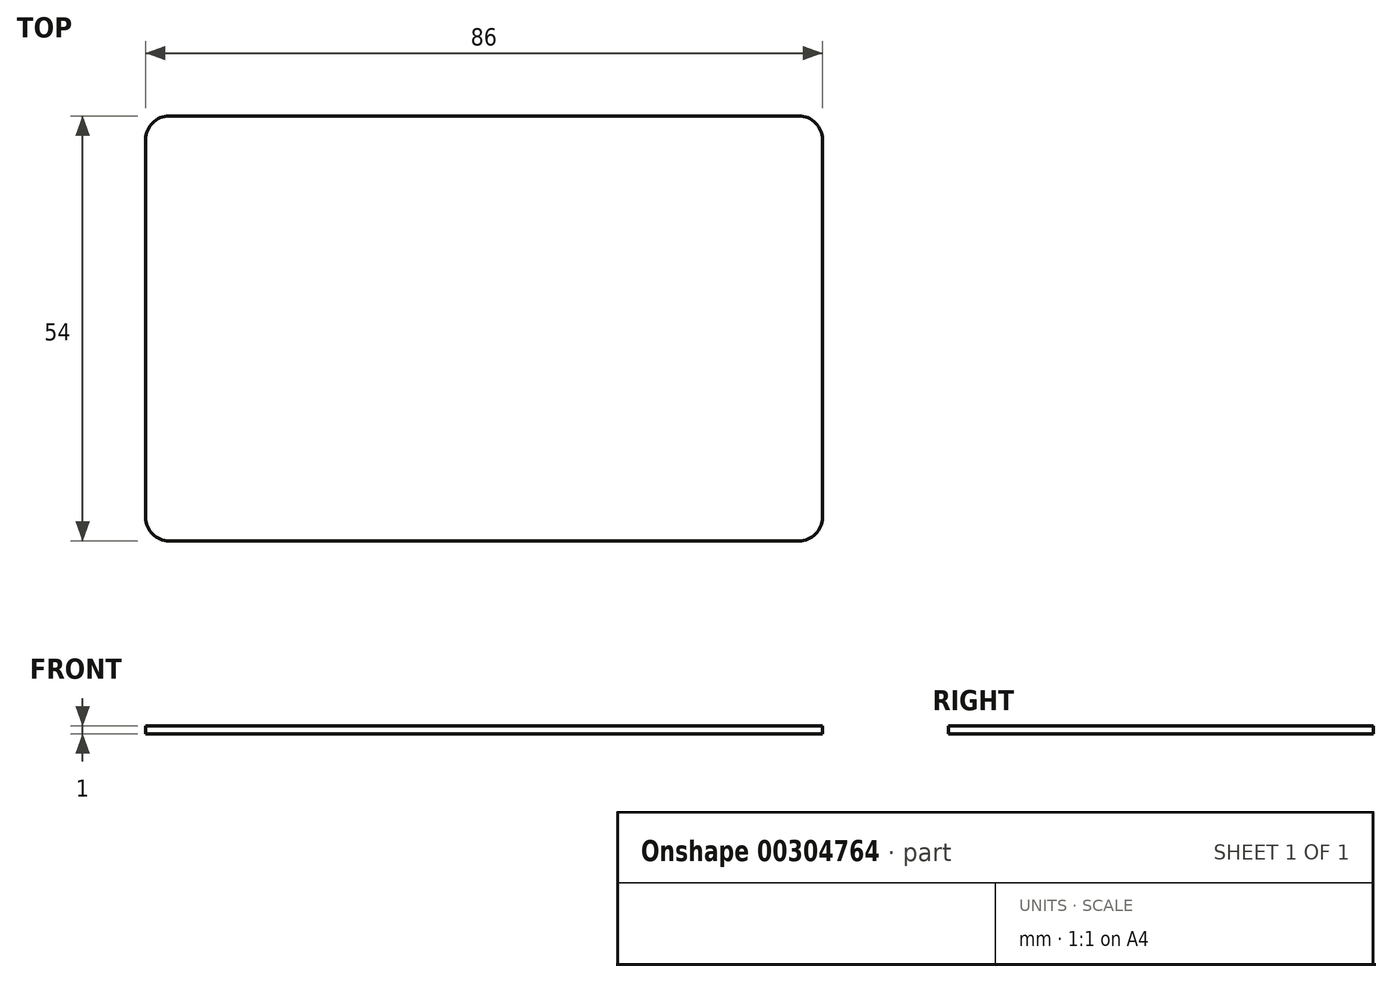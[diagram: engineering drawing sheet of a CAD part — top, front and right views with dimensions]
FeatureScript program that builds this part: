
annotation { "Feature Type Name" : "Feature", "Feature Type Description" : "" }
export const myFeature = defineFeature(function(context is Context, id is Id, definition is map)
    precondition{}
    {
        {
            var Q0;
            Q0=qCreatedBy(makeId("Top.planeOp"),FACE);
            var sketch = newSketch(context, id + "F0", { "sketchPlane" : qUnion([Q0])});
            skLineSegment(sketch, "E0.bottom", {"start": v(40, -27) * mm, "end": v(-40, -27) * mm});
            skLineSegment(sketch, "E0.top", {"start": v(40, 27) * mm, "end": v(-40, 27) * mm});
            skLineSegment(sketch, "E0.left", {"start": v(43, -24) * mm, "end": v(43, 24) * mm});
            skLineSegment(sketch, "E0.right", {"start": v(-43, -24) * mm, "end": v(-43, 24) * mm});
            skPoint(sketch, "E0.middle", {"position": v(0, 0) * mm});
            skPoint(sketch, "E1.visualSharp", {"position": v(-43, 27) * mm});
            skArc(sketch, "E1.filletArc", {"start": v(-40, 27) * mm, "mid": v(-42.12, 26.12) * mm, "end": v(-43, 24) * mm});
            skPoint(sketch, "E2.visualSharp", {"position": v(-43, -27) * mm});
            skArc(sketch, "E2.filletArc", {"start": v(-43, -24) * mm, "mid": v(-42.12, -26.12) * mm, "end": v(-40, -27) * mm});
            skPoint(sketch, "E3.visualSharp", {"position": v(43, -27) * mm});
            skArc(sketch, "E3.filletArc", {"start": v(40, -27) * mm, "mid": v(42.12, -26.12) * mm, "end": v(43, -24) * mm});
            skPoint(sketch, "E4.visualSharp", {"position": v(43, 27) * mm});
            skArc(sketch, "E4.filletArc", {"start": v(43, 24) * mm, "mid": v(42.12, 26.12) * mm, "end": v(40, 27) * mm});
            skSolve(sketch);
        }
        {
            var Q0;
            Q0=makeQuery(id+"F0.imprint","IMPRINT",FACE,{"disambiguationData":[TD([[makeQuery(id+"F0.imprint","IMPRINT",EDGE,{"derivedFrom":sQuery(id+"F0.wireOp",EDGE,"E0.bottom")}),-1.0]])]});
            extrude(context, id + "F1", {"entities" : qUnion([Q0]), "depth" : 1 * mm});
        }
    });
